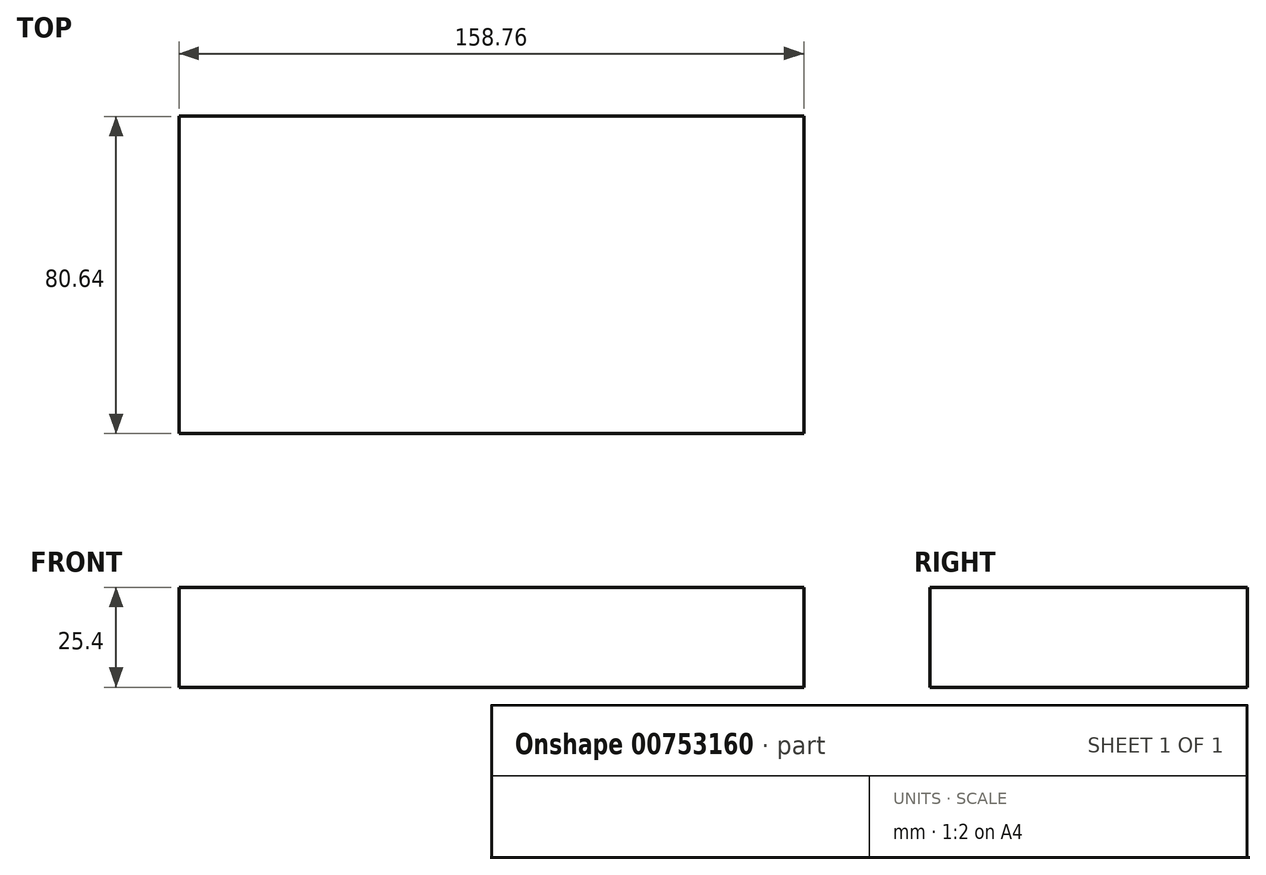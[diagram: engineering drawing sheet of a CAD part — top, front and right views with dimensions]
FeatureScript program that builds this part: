
annotation { "Feature Type Name" : "Feature", "Feature Type Description" : "" }
export const myFeature = defineFeature(function(context is Context, id is Id, definition is map)
    precondition{}
    {
        {
            var Q0;
            Q0=qCreatedBy(makeId("Top.planeOp"),FACE);
            var sketch = newSketch(context, id + "F0", { "sketchPlane" : qUnion([Q0])});
            skLineSegment(sketch, "E0.bottom", {"start": v(-79.38, 40.32) * mm, "end": v(79.38, 40.32) * mm});
            skLineSegment(sketch, "E0.top", {"start": v(-79.37, -40.32) * mm, "end": v(79.37, -40.32) * mm});
            skLineSegment(sketch, "E0.left", {"start": v(-79.37, 40.32) * mm, "end": v(-79.38, -40.32) * mm});
            skLineSegment(sketch, "E0.right", {"start": v(79.38, 40.32) * mm, "end": v(79.37, -40.32) * mm});
            skPoint(sketch, "E0.middle", {"position": v(0, 0) * mm});
            skSolve(sketch);
        }
        {
            var Q0;
            Q0 = qSketchRegion(id + "F0", true);
            extrude(context, id + "F1", {"entities" : qUnion([Q0]), "depth" : 25.4 * mm, "offsetDistance" : 25.4 * mm});
        }
    });
